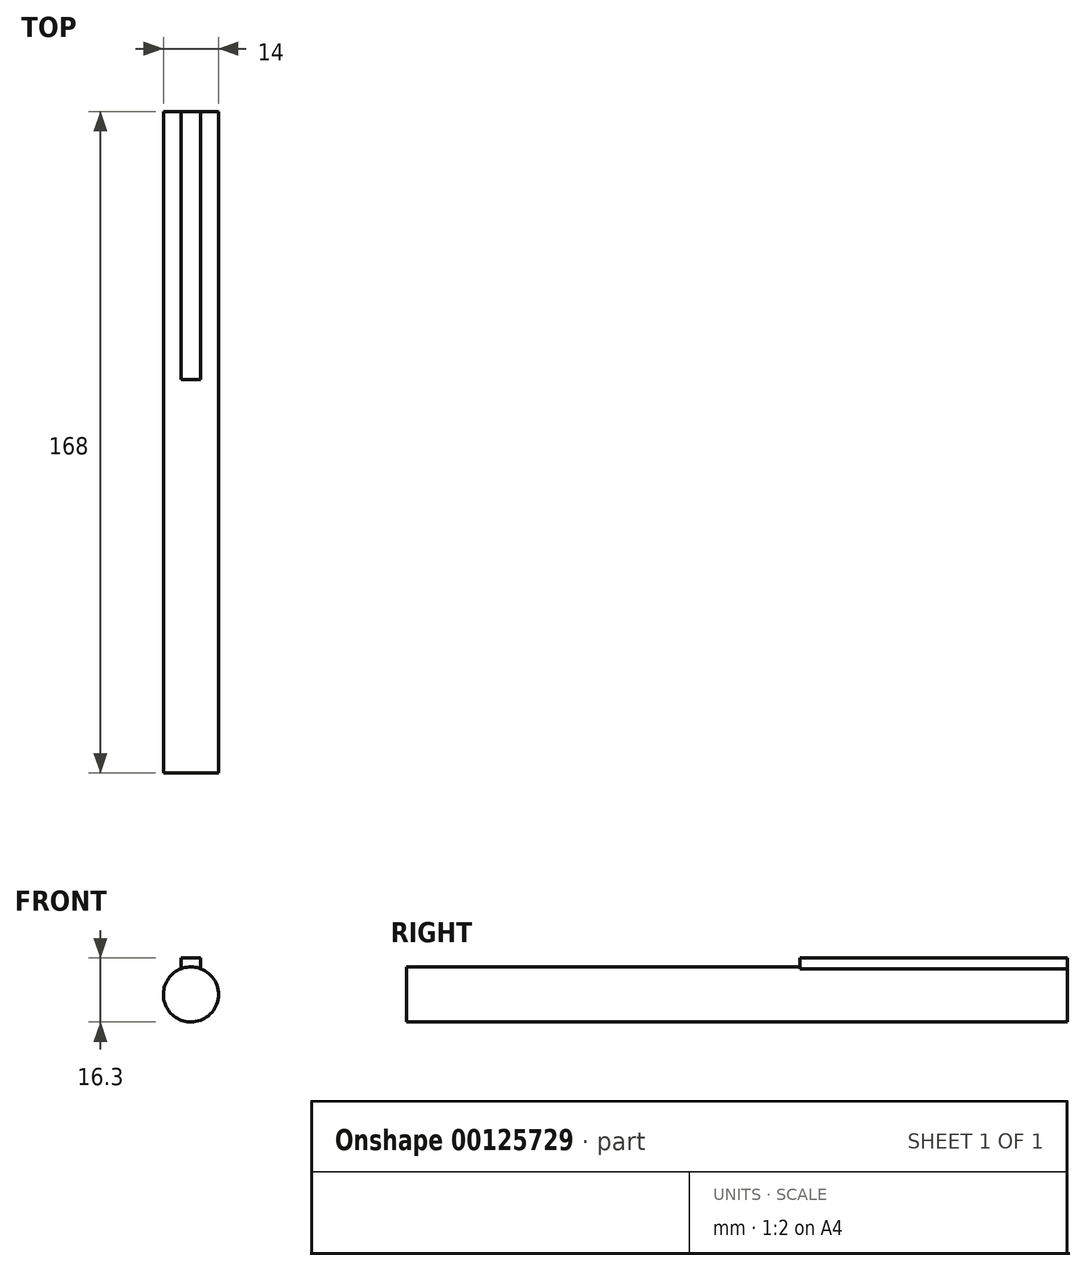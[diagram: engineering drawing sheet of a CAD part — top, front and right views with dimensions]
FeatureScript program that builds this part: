
annotation { "Feature Type Name" : "Feature", "Feature Type Description" : "" }
export const myFeature = defineFeature(function(context is Context, id is Id, definition is map)
    precondition{}
    {
        {
            var Q0;
            Q0=qCreatedBy(makeId("Front.planeOp"),FACE);
            var sketch = newSketch(context, id + "F0", { "sketchPlane" : qUnion([Q0])});
            skLineSegment(sketch, "E0.bottom", {"start": v(-2.5, 6.54) * mm, "end": v(2.5, 6.54) * mm, "construction": true});
            skLineSegment(sketch, "E0.top", {"start": v(-2.5, 9.3) * mm, "end": v(2.5, 9.3) * mm});
            skLineSegment(sketch, "E0.left", {"start": v(-2.5, 6.54) * mm, "end": v(-2.5, 9.3) * mm});
            skLineSegment(sketch, "E0.right", {"start": v(2.5, 6.54) * mm, "end": v(2.5, 9.3) * mm});
            skArc(sketch, "E1", {"start": v(-2.5, 6.54) * mm, "mid": v(0, -7) * mm, "end": v(2.5, 6.54) * mm});
            skArc(sketch, "E2", {"start": v(2.5, 6.54) * mm, "mid": v(0, 7) * mm, "end": v(-2.5, 6.54) * mm, "construction": true});
            skSolve(sketch);
        }
        {
            var Q0;
            Q0 = qSketchRegion(id + "F0", true);
            extrude(context, id + "F1", {"entities" : qUnion([Q0]), "depth" : 68 * mm, "symmetric" : true});
        }
        {
            var Q0;
            Q0=makeQuery(id+"F1.opExtrude","CAP_FACE",FACE,{"disambiguationData":[OSD([sQuery(id+"F0.wireOp",EDGE,"E0.top"),sQuery(id+"F0.wireOp",EDGE,"E0.left"),sQuery(id+"F0.wireOp",EDGE,"E0.right"),sQuery(id+"F0.wireOp",EDGE,"E1")])],"isStart":false});
            var sketch = newSketch(context, id + "F2", { "sketchPlane" : qUnion([Q0])});
            skCircle(sketch, "E3", {"center": v(0, 0) * mm, "radius": 7 * mm});
            skSolve(sketch);
        }
        {
            assignVariable(context, id + "F3", {"name" : "LRodillo", "anyValue" : 60});
        }
        {
            var Q0;
            Q0 = qSketchRegion(id + "F2", true);
            extrude(context, id + "F4", {"entities" : qUnion([Q0]), "operationType" : NewBodyOperationType.ADD, "depth" : (40 + getVariable(context, 'LRodillo')) * mm});
        }
    });
